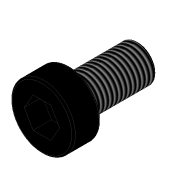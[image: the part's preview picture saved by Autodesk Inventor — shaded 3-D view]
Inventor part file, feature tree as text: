
AUTODESK INVENTOR PART (.ipt)
format: ipt  version: 2020 (Build 240168000, 168)  size: 128,000 bytes
history: native  units: mm
features: extrude x3, sketch x3, fillet x1, thread x1
ambient origin geometry x8: Origin, YZ Plane, XZ Plane, XY Plane, X Axis, Y Axis, Z Axis, Center Point
bodies: Solid1 (feature_tree)
feature tree (8):
  extrude  "Extrusion1"  Depth=3.35mm
  extrude  "Extrusion2"  Depth=1.0mm TaperAngle=0.0deg
  extrude  "Extrusion3"  Depth=7.5mm TaperAngle=0.0deg
  fillet  "Fillet1"  Radius=0.2mm
  thread  "Thread1"  [1 undecoded]
  sketch  "Sketch1"  dims[d0=6.9mm d1=3.35mm]
  sketch  "Sketch2"  dims[d2=2.0mm d3=0.0mm d4=1.0mm d5=0.0mm]
  sketch  "Sketch3"  dims[d6=4.0mm d7=7.5mm d8=0.0mm d9=0.2mm d10=7.3mm d11=0.0mm]
note: 1 required parameter value undecoded (feature->parameter linkage not recoverable at this tier; creation-order binding heuristic only, values carry confidence <= 0.55)
